# Revit family: Faucet-Deck_Mount-Bath-KOHLER-BELLERA-K-T26428_1
name_source: partatom
category: Plumbing Fixtures
revit_build: Autodesk Revit 2017 (Build: 20160225_1515(x64)
units: mm (PartAtom-declared; Revit-internal decimal feet)

## family parameters
Cut with Voids When Loaded = No
Host = Face
OmniClass Number = 23.31.11.00
OmniClass Title = Faucets
Part Type = Normal
Room Calculation Point = No
Round Connector Dimension = Use Diameter
Shared = No

## types (3) — shared parameters
ADA Compliant = No
Assembly Code = D2010
CW Connection = Yes
Cold Water Inlet = Cold Water Inlet
Date Modified = 09/23/2021
Default Elevation = 36"
Description = 2H DCK-MNT FCT TRIM
Drain Included = No
Flow Rate = 0 GPM
HW Connection = Yes
Handle Clearance = 3 5/8"
Handle Height = 3 3/4"
Height = 10 9/16"
Hot Water Inlet = Hot Water Inlet
Length = 7 5/8"
Manufacturer = KOHLER Co.
Master Format 2014 = 22 41 39
Master Format 2014 Name = Residential Faucets, Supplies, and Trim
Material = Premium Metal Construction
Pressure = 0.00 psi
Product Documentation Link = https://www.us.kohler.com
Product Name = BELLERA
Product Page URL = http://www.us.kohler.com
Spout Reach = 7 5/8"
URL = https://www.us.kohler.com
Vent Connection = No
Waste Connection = No
Waste Water Outlet = Waste Water Outlet
WaterSense Certified = No

## per-type parameters (varying)
| type | Finish | Model | Plug Screw Finish | Type |
| CP-Polished Chrome | Kohler-Metal-CP-Polished_Chrome | K-T26428-4-CP | Kohler-Plastic-58-Thunder_Grey | 1 |
| BN-Vibrant Brushed Nickel | Kohler-Metal-BN-Vibrant_Brushed_Nickel | K-T26428-4-BN | Kohler-Plastic-58-Thunder_Grey | 2 |
| 2BZ-Oil Rubbed Bronze | Kohler-Metal-2BZ-Oil_Rubbed_Bronze | K-T26428-4-2BZ | Kohler-Plastic-7-Black_Black | 3 |

## geometry (parser evidence)
native form markers: Sweep x8
no freeform markers — native parametric forms only
